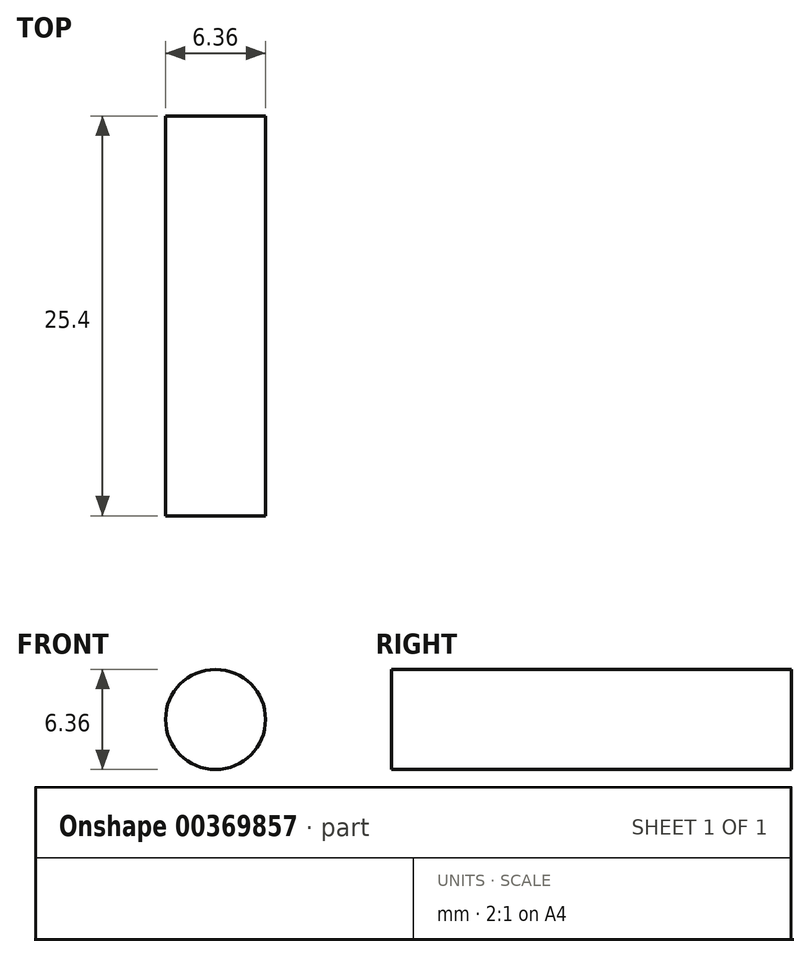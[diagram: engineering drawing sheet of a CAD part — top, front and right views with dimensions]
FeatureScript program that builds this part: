
annotation { "Feature Type Name" : "Feature", "Feature Type Description" : "" }
export const myFeature = defineFeature(function(context is Context, id is Id, definition is map)
    precondition{}
    {
        {
            var Q0;
            Q0=qCreatedBy(makeId("Front.planeOp"),FACE);
            var sketch = newSketch(context, id + "F0", { "sketchPlane" : qUnion([Q0])});
            skCircle(sketch, "E0", {"center": v(0, 0) * mm, "radius": 3.18 * mm});
            skSolve(sketch);
        }
        {
            var Q0;
            Q0 = qSketchRegion(id + "F0", true);
            extrude(context, id + "F1", {"entities" : qUnion([Q0]), "depth" : 25.4 * mm});
        }
    });
